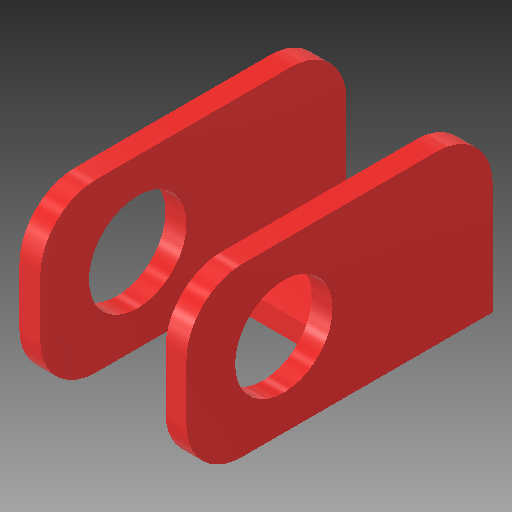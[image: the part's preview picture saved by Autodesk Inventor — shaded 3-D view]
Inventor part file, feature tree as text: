
AUTODESK INVENTOR PART (.ipt)
format: ipt  version: 2017 SP1 (Build 210196100, 196)  size: 176,640 bytes
history: native  units: in
note: dims shown in document units (in); Inventor stores cm internally (conversion verified against a paired STEP export)
features: extrude x3, sketch x3, fillet x1
ambient origin geometry x8: Origin, YZ Plane, XZ Plane, XY Plane, X Axis, Y Axis, Z Axis, Center Point
bodies: Solid1 (feature_tree)
feature tree (7):
  extrude  "Extrusion1"  Depth=1.5in
  extrude  "Extrusion2"  Depth=2.75in TaperAngle=0.0deg
  extrude  "Extrusion3"  Depth=0.75in
  fillet  "Fillet1"  Radius=0.75in
  sketch  "Sketch1"  dims[d0=0.1875in d2=1.5in]
  sketch  "Sketch2"  dims[d3=1.5in d4=2.75in d5=0.0in]
  sketch  "Sketch3"  dims[d6=0.2in d7=0.75in d8=0.75in d10=0.5625in d11=2.5in d12=0.0in d13=0.875in d14=0.75in d15=1.125in d16=1.3125in d17=2.5in d18=0.0in d19=0.5in d21=0.1875in d22=0.1875in]
